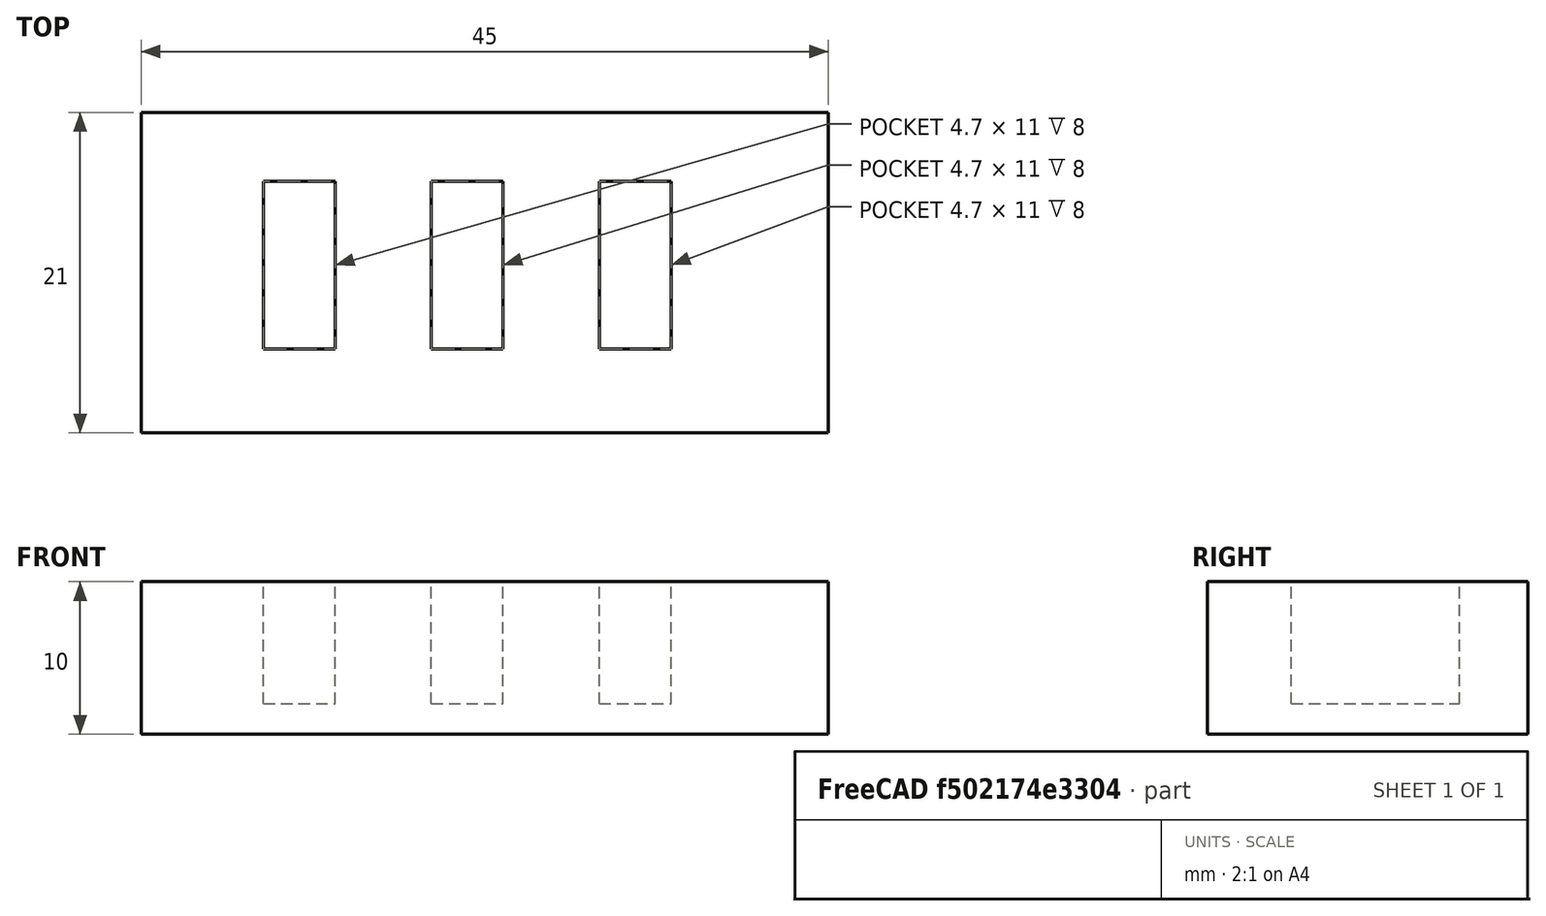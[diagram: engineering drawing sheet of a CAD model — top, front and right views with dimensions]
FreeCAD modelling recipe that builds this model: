
FCSTD DOCUMENT  (FreeCAD 1.0R39319 (Git))
Label: ojt1_t08p01_usb_flash
License: All rights reserved
LicenseURL: https://en.wikipedia.org/wiki/All_rights_reserved
objects: Part::Box×4, Part::Cut×3
note: 7 computed .brp shape members not serialized (recipe doc carries the construction recipe); baked Part::Feature solids carry a one-line shape summary decoded from their .brp

FEATURE [Part::Box] Box  label="Cub"
  AttacherType = Attacher::AttachEngine3D
  Height = 10
  Length = 45
  Width = 21
FEATURE [Part::Box] Box001  label="Cub001"
  AttacherType = Attacher::AttachEngine3D
  Height = 8.5
  Length = 4.7
  Placement = pos=(8,5.5,2) rot=(0,0,1;0rad)
  Width = 11
FEATURE [Part::Box] Box002  label="Cub002"
  AttacherType = Attacher::AttachEngine3D
  Height = 8.5
  Length = 4.7
  Placement = pos=(19,5.5,2) rot=(0,0,1;0rad)
  Width = 11
FEATURE [Part::Box] Box003  label="Cub003"
  AttacherType = Attacher::AttachEngine3D
  Height = 8.5
  Length = 4.7
  Placement = pos=(30,5.5,2) rot=(0,0,1;0rad)
  Width = 11
FEATURE [Part::Cut] Cut
  Base = -> Box
  Refine = true
  Tool = -> Box001
FEATURE [Part::Cut] Cut001
  Base = -> Cut
  Refine = true
  Tool = -> Box003
FEATURE [Part::Cut] Cut002
  Base = -> Cut001
  Refine = true
  Tool = -> Box002
